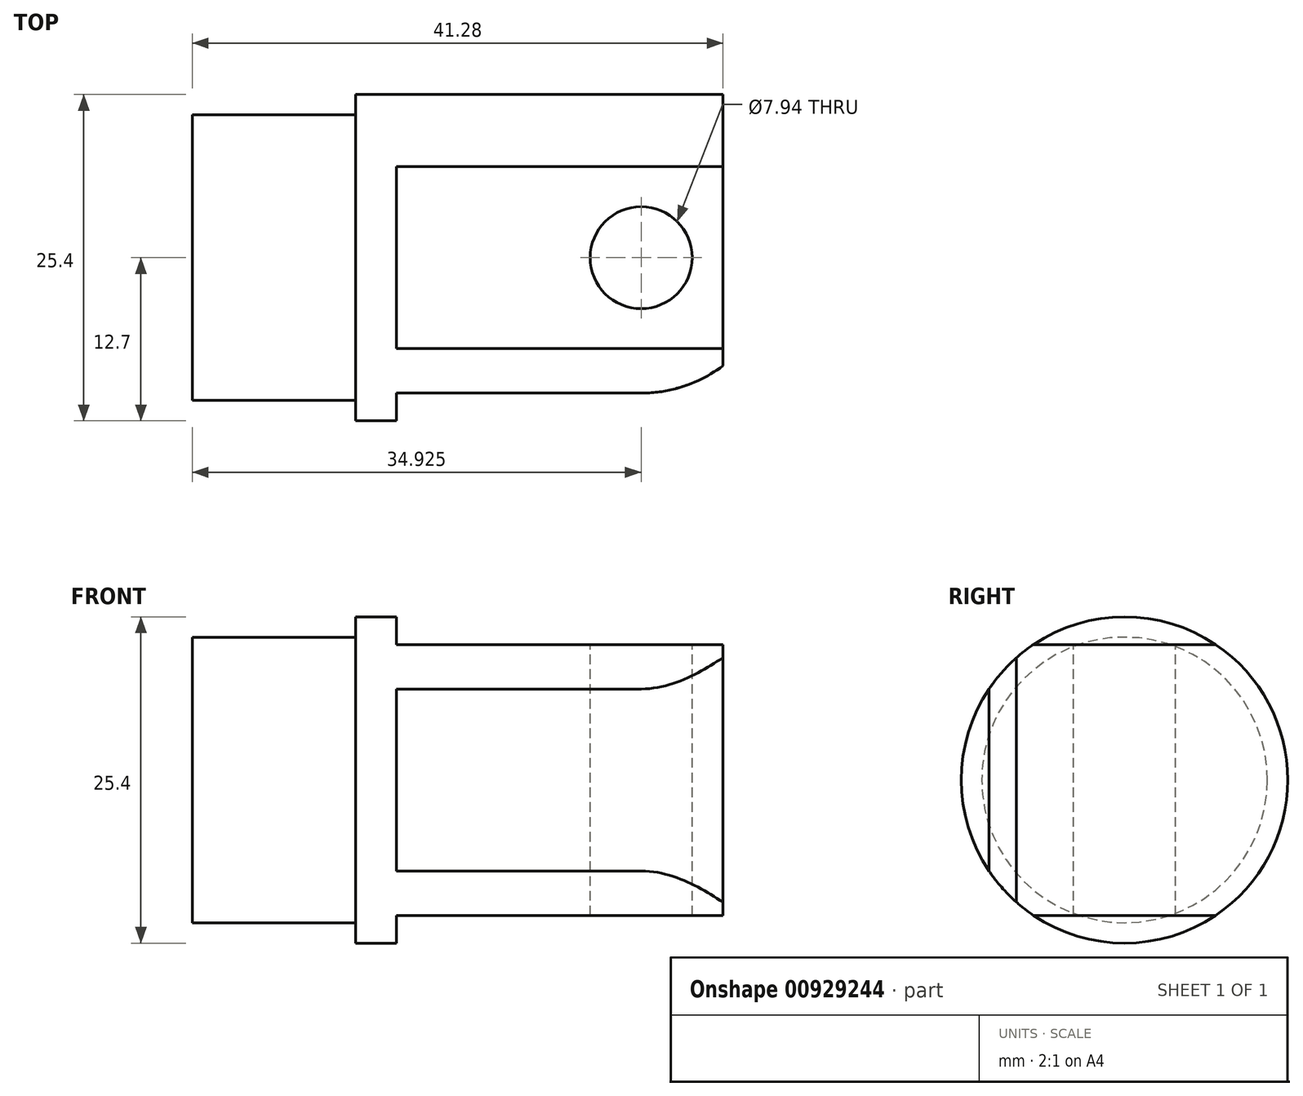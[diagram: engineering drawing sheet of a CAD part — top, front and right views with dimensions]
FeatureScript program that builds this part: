
annotation { "Feature Type Name" : "Feature", "Feature Type Description" : "" }
export const myFeature = defineFeature(function(context is Context, id is Id, definition is map)
    precondition{}
    {
        {
            var Q0;
            Q0=qCreatedBy(makeId("Right.planeOp"),FACE);
            var sketch = newSketch(context, id + "F0", { "sketchPlane" : qUnion([Q0])});
            skCircle(sketch, "E0", {"center": v(0, 0) * mm, "radius": 12.7 * mm});
            skSolve(sketch);
        }
        {
            var Q0;
            Q0=makeQuery(id+"F0.imprint","IMPRINT",FACE,{"disambiguationData":[TD([[makeQuery(id+"F0.imprint","IMPRINT",EDGE,{"derivedFrom":sQuery(id+"F0.wireOp",EDGE,"E0")}),1.0]])]});
            extrude(context, id + "F1", {"entities" : qUnion([Q0]), "depth" : 28.57 * mm, "offsetDistance" : 25.4 * mm});
        }
        {
            var Q0;
            Q0=makeQuery(id+"F1.opExtrude","CAP_FACE",FACE,{"disambiguationData":[OSD([sQuery(id+"F0.wireOp",EDGE,"E0")])],"isStart":true});
            var sketch = newSketch(context, id + "F2", { "sketchPlane" : qUnion([Q0])});
            skCircle(sketch, "E1", {"center": v(0, 0) * mm, "radius": 11.11 * mm});
            skSolve(sketch);
        }
        {
            var Q0;
            Q0=makeQuery(id+"F2.imprint","IMPRINT",FACE,{"disambiguationData":[TD([[makeQuery(id+"F2.imprint","IMPRINT",EDGE,{"derivedFrom":sQuery(id+"F2.wireOp",EDGE,"E1")}),1.0]])]});
            extrude(context, id + "F3", {"entities" : qUnion([Q0]), "operationType" : NewBodyOperationType.ADD, "depth" : 12.7 * mm, "offsetDistance" : 25.4 * mm});
        }
        {
            var Q0;
            Q0=makeQuery(id+"F1.opExtrude","CAP_FACE",FACE,{"disambiguationData":[OSD([sQuery(id+"F0.wireOp",EDGE,"E0")])],"isStart":false});
            var sketch = newSketch(context, id + "F4", { "sketchPlane" : qUnion([Q0])});
            skLineSegment(sketch, "E2.bottom", {"start": v(-10.54, 10.54) * mm, "end": v(14.62, 10.54) * mm});
            skLineSegment(sketch, "E2.top", {"start": v(-10.54, -10.54) * mm, "end": v(14.62, -10.54) * mm});
            skLineSegment(sketch, "E2.left", {"start": v(-10.54, 10.54) * mm, "end": v(-10.54, -10.54) * mm});
            skPoint(sketch, "E2.middle", {"position": v(0, 0) * mm});
            skLineSegment(sketch, "E3.bottom", {"start": v(-14.62, 13.39) * mm, "end": v(14.62, 13.39) * mm});
            skLineSegment(sketch, "E3.top", {"start": v(-14.62, -13.39) * mm, "end": v(14.62, -13.39) * mm});
            skLineSegment(sketch, "E3.left", {"start": v(-14.62, 13.39) * mm, "end": v(-14.62, -13.39) * mm});
            skLineSegment(sketch, "E3.right", {"start": v(14.62, 13.39) * mm, "end": v(14.62, 10.54) * mm});
            skPoint(sketch, "E4.orphan", {"position": v(10.54, 10.54) * mm});
            skPoint(sketch, "E5.orphan", {"position": v(10.54, -10.54) * mm});
            skLineSegment(sketch, "E6.trimOffspring", {"start": v(14.62, -10.54) * mm, "end": v(14.62, -13.39) * mm});
            skSolve(sketch);
        }
        {
            var Q0;
            Q0=makeQuery(id+"F4.imprint","IMPRINT",FACE,{"disambiguationData":[TD([[makeQuery(id+"F4.imprint","IMPRINT",EDGE,{"derivedFrom":sQuery(id+"F4.wireOp",EDGE,"E3.bottom")}),-1.0]])]});
            var Q1;
            {var subQ0=sQuery(id+"F4.wireOp",EDGE,"E2.bottom");var subQ1=makeQuery(id+"F1.opExtrude","CAP_EDGE",EDGE,{"disambiguationData":[OSD([sQuery(id+"F0.wireOp",EDGE,"E0")])],"isStart":false});var subQ2=makeQuery(id+"F4.imprint","INTERSECT",VERTEX,{"disambiguationData":[OD(0.0)],"derivedFrom":[subQ1,subQ0]});Q1=makeQuery(id+"F4.imprint","IMPRINT",FACE,{"disambiguationData":[TD([[makeQuery(id+"F4.imprint","IMPRINT",EDGE,{"disambiguationData":[TD([[subQ2,1.0]])],"derivedFrom":subQ0}),1.0]])]});}
            var Q2;
            {var subQ0=sQuery(id+"F4.wireOp",EDGE,"E2.left");var subQ1=makeQuery(id+"F1.opExtrude","CAP_EDGE",EDGE,{"disambiguationData":[OSD([sQuery(id+"F0.wireOp",EDGE,"E0")])],"isStart":false});var subQ2=makeQuery(id+"F4.imprint","INTERSECT",VERTEX,{"disambiguationData":[OD(0.0)],"derivedFrom":[subQ1,subQ0]});Q2=makeQuery(id+"F4.imprint","IMPRINT",FACE,{"disambiguationData":[TD([[makeQuery(id+"F4.imprint","IMPRINT",EDGE,{"disambiguationData":[TD([[subQ2,-1.0]])],"derivedFrom":subQ0}),-1.0]])]});}
            var Q3;
            {var subQ0=sQuery(id+"F4.wireOp",EDGE,"E2.top");var subQ1=makeQuery(id+"F1.opExtrude","CAP_EDGE",EDGE,{"disambiguationData":[OSD([sQuery(id+"F0.wireOp",EDGE,"E0")])],"isStart":false});var subQ2=makeQuery(id+"F4.imprint","INTERSECT",VERTEX,{"disambiguationData":[OD(0.0)],"derivedFrom":[subQ1,subQ0]});Q3=makeQuery(id+"F4.imprint","IMPRINT",FACE,{"disambiguationData":[TD([[makeQuery(id+"F4.imprint","IMPRINT",EDGE,{"disambiguationData":[TD([[subQ2,1.0]])],"derivedFrom":subQ0}),-1.0]])]});}
            extrude(context, id + "F5", {"entities" : qUnion([Q0, Q1, Q2, Q3]), "operationType" : NewBodyOperationType.REMOVE, "oppositeDirection" : true, "depth" : 25.4 * mm, "offsetDistance" : 25.4 * mm});
        }
        {
            var Q0;
            Q0=makeQuery(id+"F5.boolean.opBoolean","COPY",FACE,{"derivedFrom":makeQuery(id+"F5.opExtrude","SWEPT_FACE",FACE,{"disambiguationData":[OSD([sQuery(id+"F4.wireOp",EDGE,"E2.bottom")])]})});
            var sketch = newSketch(context, id + "F6", { "sketchPlane" : qUnion([Q0])});
            skCircle(sketch, "E7", {"center": v(22.23, 0) * mm, "radius": 3.97 * mm});
            skSolve(sketch);
        }
        {
            var Q0;
            Q0=makeQuery(id+"F6.imprint","IMPRINT",FACE,{"disambiguationData":[TD([[makeQuery(id+"F6.imprint","IMPRINT",EDGE,{"derivedFrom":sQuery(id+"F6.wireOp",EDGE,"E7")}),1.0]])]});
            extrude(context, id + "F7", {"entities" : qUnion([Q0]), "operationType" : NewBodyOperationType.REMOVE, "endBound" : BoundingType.THROUGH_ALL, "oppositeDirection" : true, "depth" : 25.4 * mm, "offsetDistance" : 25.4 * mm});
        }
        {
            var Q0;
            Q0=makeQuery(id+"F5.boolean.opBoolean","COPY",FACE,{"derivedFrom":makeQuery(id+"F5.opExtrude","SWEPT_FACE",FACE,{"disambiguationData":[OSD([sQuery(id+"F4.wireOp",EDGE,"E2.bottom")])]})});
            var sketch = newSketch(context, id + "F8", { "sketchPlane" : qUnion([Q0])});
            skArc(sketch, "E8", {"start": v(22.22, -10.54) * mm, "mid": v(29.68, -7.45) * mm, "end": v(32.77, 0) * mm});
            skArc(sketch, "E9", {"start": v(22.22, -14.3) * mm, "mid": v(32.33, -10.1) * mm, "end": v(36.52, 0) * mm});
            skLineSegment(sketch, "E10", {"start": v(22.23, -10.54) * mm, "end": v(22.23, -14.3) * mm});
            skLineSegment(sketch, "E11", {"start": v(32.77, 0) * mm, "end": v(36.52, 0) * mm});
            skSolve(sketch);
        }
        {
            var Q0;
            Q0=makeQuery(id+"F8.imprint","IMPRINT",FACE,{"disambiguationData":[TD([[makeQuery(id+"F8.imprint","IMPRINT",EDGE,{"derivedFrom":sQuery(id+"F8.wireOp",EDGE,"E8")}),-1.0]])]});
            extrude(context, id + "F9", {"entities" : qUnion([Q0]), "operationType" : NewBodyOperationType.REMOVE, "endBound" : BoundingType.THROUGH_ALL, "oppositeDirection" : true, "depth" : 25.4 * mm, "offsetDistance" : 25.4 * mm});
        }
    });
